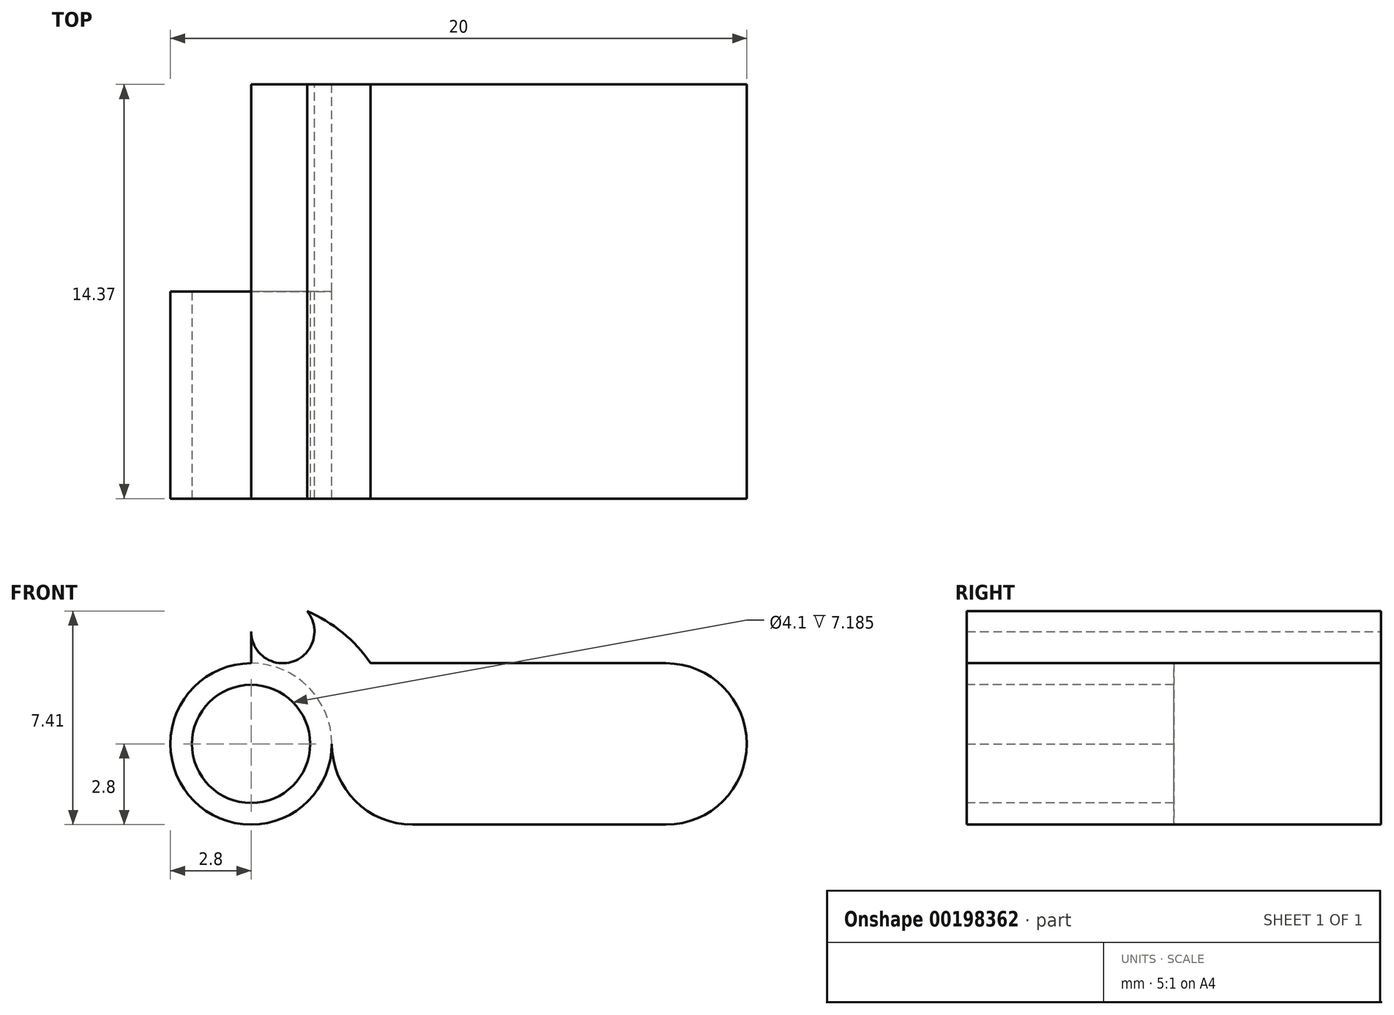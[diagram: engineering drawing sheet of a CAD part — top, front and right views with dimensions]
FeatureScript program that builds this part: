
annotation { "Feature Type Name" : "Feature", "Feature Type Description" : "" }
export const myFeature = defineFeature(function(context is Context, id is Id, definition is map)
    precondition{}
    {
        {
            var Q0;
            Q0=qCreatedBy(makeId("Front.planeOp"),FACE);
            var sketch = newSketch(context, id + "F0", { "sketchPlane" : qUnion([Q0])});
            skLineSegment(sketch, "E0.bottom", {"start": v(2.8, 0) * mm, "end": v(17.2, 0) * mm});
            skLineSegment(sketch, "E0.top", {"start": v(2.8, 5.6) * mm, "end": v(17.2, 5.6) * mm});
            skLineSegment(sketch, "E1.bottom", {"start": v(17.2, 5.6) * mm, "end": v(14.4, 5.6) * mm, "construction": true});
            skLineSegment(sketch, "E1.top", {"start": v(17.2, 0) * mm, "end": v(14.4, 0) * mm, "construction": true});
            skLineSegment(sketch, "E1.right", {"start": v(14.4, 5.6) * mm, "end": v(14.4, 0) * mm, "construction": true});
            skLineSegment(sketch, "E2", {"start": v(14.4, 5.6) * mm, "end": v(20, 0) * mm, "construction": true});
            skArc(sketch, "E3", {"start": v(17.2, 5.6) * mm, "mid": v(14.4, 2.8) * mm, "end": v(17.2, 0) * mm});
            skArc(sketch, "E4", {"start": v(17.2, 4.8) * mm, "mid": v(15.2, 2.8) * mm, "end": v(17.2, 0.8) * mm});
            skArc(sketch, "E5", {"start": v(12.74, 5.05) * mm, "mid": v(15.93, 0.46) * mm, "end": v(13, 5.22) * mm, "construction": true});
            skArc(sketch, "E6", {"start": v(11.6, 0) * mm, "mid": v(13.58, 0.82) * mm, "end": v(14.4, 2.8) * mm});
            skLineSegment(sketch, "E7", {"start": v(10, 5.6) * mm, "end": v(10, 0) * mm, "construction": true});
            skLineSegment(sketch, "E8", {"start": v(17.2, 2.8) * mm, "end": v(17.2, 5.6) * mm, "construction": true});
            skPoint(sketch, "E8.endSnap0", {"position": v(17.2, 5.6) * mm});
            skCircle(sketch, "E9", {"center": v(17.2, 6.7) * mm, "radius": 1.1 * mm, "construction": true});
            skPoint(sketch, "E10.orphan", {"position": v(20, 5.6) * mm});
            skPoint(sketch, "E11.orphan", {"position": v(17.2, 7.8) * mm});
            skArc(sketch, "E12.trimOffspring", {"start": v(13, 5.22) * mm, "mid": v(12.93, 5.26) * mm, "end": v(12.87, 5.3) * mm});
            skArc(sketch, "E13.MirrorCS", {"start": v(7, 5.22) * mm, "mid": v(7.07, 5.26) * mm, "end": v(7.13, 5.3) * mm});
            skLineSegment(sketch, "E14.MirrorCS", {"start": v(2.8, 6.7) * mm, "end": v(2.8, 5.6) * mm});
            skPoint(sketch, "E15.MirrorP", {"position": v(2.8, 5.6) * mm});
            skArc(sketch, "E16.MirrorCS", {"start": v(8.4, 0) * mm, "mid": v(6.42, 0.82) * mm, "end": v(5.6, 2.8) * mm});
            skPoint(sketch, "E17.MirrorP", {"position": v(2.8, 7.8) * mm});
            skArc(sketch, "E18.MirrorCS", {"start": v(7.26, 5.05) * mm, "mid": v(4.07, 0.46) * mm, "end": v(7, 5.22) * mm, "construction": true});
            skCircle(sketch, "E19.MirrorC", {"center": v(2.8, 2.8) * mm, "radius": 2 * mm});
            skArc(sketch, "E20.MirrorCS", {"start": v(3.55, 7.74) * mm, "mid": v(5.47, 7.03) * mm, "end": v(6.94, 5.6) * mm});
            skLineSegment(sketch, "E21.MirrorCS", {"start": v(2.8, 2.8) * mm, "end": v(2.8, 6.7) * mm, "construction": true});
            skPoint(sketch, "E22.MirrorP", {"position": v(0, 5.6) * mm});
            skArc(sketch, "E23.MirrorCS", {"start": v(4.74, 7.4) * mm, "mid": v(3.6, 5.64) * mm, "end": v(3.55, 7.74) * mm});
            skCircle(sketch, "E24.MirrorC", {"center": v(2.8, 2.8) * mm, "radius": 2.8 * mm});
            skCircle(sketch, "E25.MirrorC", {"center": v(2.8, 6.7) * mm, "radius": 1.1 * mm, "construction": true});
            skLineSegment(sketch, "E26.MirrorCS", {"start": v(2.8, 5.6) * mm, "end": v(5.6, 5.6) * mm, "construction": true});
            skLineSegment(sketch, "E27.MirrorCS", {"start": v(5.6, 5.6) * mm, "end": v(0, 0) * mm, "construction": true});
            skLineSegment(sketch, "E28.MirrorCS", {"start": v(2.8, 0) * mm, "end": v(5.6, 0) * mm, "construction": true});
            skLineSegment(sketch, "E29.MirrorCS", {"start": v(5.6, 5.6) * mm, "end": v(5.6, 0) * mm, "construction": true});
            skPoint(sketch, "E30.orphan", {"position": v(0, 0) * mm});
            skPoint(sketch, "E31.orphan", {"position": v(13.06, 5.6) * mm});
            skPoint(sketch, "E32.end.orphan", {"position": v(15.26, 7.4) * mm});
            skPoint(sketch, "E33.trimOffspring.end.orphan", {"position": v(16.45, 7.74) * mm});
            skPoint(sketch, "E34.center.orphan", {"position": v(16.1, 6.7) * mm});
            skLineSegment(sketch, "E35", {"start": v(17.2, 5.6) * mm, "end": v(17.2, 0) * mm});
            skCircle(sketch, "E36", {"center": v(17.2, 2.8) * mm, "radius": 2.8 * mm});
            skSolve(sketch);
        }
        {
            var Q0;
            {var subQ7=sQuery(id+"F0.wireOp",EDGE,"E6");Q0=makeQuery(id+"F0.imprint","IMPRINT",FACE,{"disambiguationData":[TD([[makeQuery(id+"F0.imprint","IMPRINT",EDGE,{"derivedFrom":subQ7}),1.0]])]});}
            var Q1;
            {var subQ0=sQuery(id+"F0.wireOp",EDGE,"E4");Q1=makeQuery(id+"F0.imprint","IMPRINT",FACE,{"disambiguationData":[TD([[makeQuery(id+"F0.imprint","IMPRINT",EDGE,{"derivedFrom":subQ0}),-1.0]])]});}
            var Q2;
            {var subQ0=sQuery(id+"F0.wireOp",EDGE,"E4");Q2=makeQuery(id+"F0.imprint","IMPRINT",FACE,{"disambiguationData":[TD([[makeQuery(id+"F0.imprint","IMPRINT",EDGE,{"derivedFrom":subQ0}),1.0]])]});}
            var Q3;
            {var subQ3=sQuery(id+"F0.wireOp",EDGE,"E6");Q3=makeQuery(id+"F0.imprint","IMPRINT",FACE,{"disambiguationData":[TD([[makeQuery(id+"F0.imprint","IMPRINT",EDGE,{"derivedFrom":subQ3}),-1.0]])]});}
            var Q4;
            {var subQ0=sQuery(id+"F0.wireOp",EDGE,"E23.MirrorCS");var subQ1=sQuery(id+"F0.wireOp",EDGE,"E20.MirrorCS");var subQ2=makeQuery(id+"F0.imprint","INTERSECT",VERTEX,{"disambiguationData":[OD(0.0)],"derivedFrom":[subQ1,subQ0]});Q4=makeQuery(id+"F0.imprint","IMPRINT",FACE,{"disambiguationData":[TD([[makeQuery(id+"F0.imprint","IMPRINT",EDGE,{"disambiguationData":[TD([[subQ2,-1.0]])],"derivedFrom":subQ1}),-1.0]])]});}
            var Q5;
            {var subQ0=sQuery(id+"F0.wireOp",EDGE,"E20.MirrorCS");var subQ1=sQuery(id+"F0.wireOp",EDGE,"E0.top");var subQ2=makeQuery(id+"F0.imprint","INTERSECT",VERTEX,{"derivedFrom":[subQ1,subQ0]});Q5=makeQuery(id+"F0.imprint","IMPRINT",FACE,{"disambiguationData":[TD([[makeQuery(id+"F0.imprint","IMPRINT",EDGE,{"disambiguationData":[TD([[subQ2,1.0]])],"derivedFrom":subQ1}),1.0]])]});}
            var Q6;
            {var subQ0=sQuery(id+"F0.wireOp",EDGE,"E14.MirrorCS");Q6=makeQuery(id+"F0.imprint","IMPRINT",FACE,{"disambiguationData":[TD([[makeQuery(id+"F0.imprint","IMPRINT",EDGE,{"derivedFrom":subQ0}),1.0]])]});}
            var Q7;
            {var subQ1=sQuery(id+"F0.wireOp",EDGE,"E35");var subQ3=sQuery(id+"F0.wireOp",EDGE,"E4");var subQ4=makeQuery(id+"F0.imprint","INTERSECT",VERTEX,{"disambiguationData":[OD(0.0)],"derivedFrom":[subQ3,subQ1]});Q7=makeQuery(id+"F0.imprint","IMPRINT",FACE,{"disambiguationData":[TD([[makeQuery(id+"F0.imprint","IMPRINT",EDGE,{"disambiguationData":[TD([[subQ4,-1.0]])],"derivedFrom":subQ1}),1.0]])]});}
            extrude(context, id + "F1", {"entities" : qUnion([Q0, Q1, Q2, Q3, Q4, Q5, Q6, Q7]), "depth" : 14.37 * mm});
        }
        {
            var Q0;
            Q0=makeQuery(id+"F1.opExtrude","CAP_FACE",FACE,{"disambiguationData":[OSD([sQuery(id+"F0.wireOp",EDGE,"E0.bottom"),sQuery(id+"F0.wireOp",EDGE,"E0.top"),sQuery(id+"F0.wireOp",EDGE,"E14.MirrorCS"),sQuery(id+"F0.wireOp",EDGE,"E16.MirrorCS"),sQuery(id+"F0.wireOp",EDGE,"E20.MirrorCS"),sQuery(id+"F0.wireOp",EDGE,"E23.MirrorCS"),sQuery(id+"F0.wireOp",EDGE,"E24.MirrorC"),sQuery(id+"F0.wireOp",EDGE,"E35")])],"isStart":false});
            var sketch = newSketch(context, id + "F2", { "sketchPlane" : qUnion([Q0])});
            skLineSegment(sketch, "E37", {"start": v(5.6, 2.8) * mm, "end": v(2.8, 2.8) * mm, "construction": true});
            skCircle(sketch, "E38", {"center": v(2.8, 2.8) * mm, "radius": 2.8 * mm});
            skCircle(sketch, "E39", {"center": v(2.8, 2.8) * mm, "radius": 2.05 * mm});
            skArc(sketch, "E40", {"start": v(5.6, 2.8) * mm, "mid": v(6.42, 0.82) * mm, "end": v(8.4, 0) * mm});
            skLineSegment(sketch, "E41", {"start": v(2.8, 0) * mm, "end": v(8.4, 0) * mm});
            skSolve(sketch);
        }
        {
            var Q0;
            Q0=makeQuery(id+"F2.imprint","IMPRINT",FACE,{"disambiguationData":[TD([[makeQuery(id+"F2.imprint","IMPRINT",EDGE,{"derivedFrom":sQuery(id+"F2.wireOp",EDGE,"E39")}),-1.0]])]});
            var Q1;
            {var subQ0=sQuery(id+"F2.wireOp",EDGE,"E40");Q1=makeQuery(id+"F2.imprint","IMPRINT",FACE,{"disambiguationData":[TD([[makeQuery(id+"F2.imprint","IMPRINT",EDGE,{"derivedFrom":subQ0}),1.0]])]});}
            extrude(context, id + "F3", {"entities" : qUnion([Q0, Q1]), "operationType" : NewBodyOperationType.ADD, "oppositeDirection" : true, "depth" : 7.18 * mm});
        }
    });
